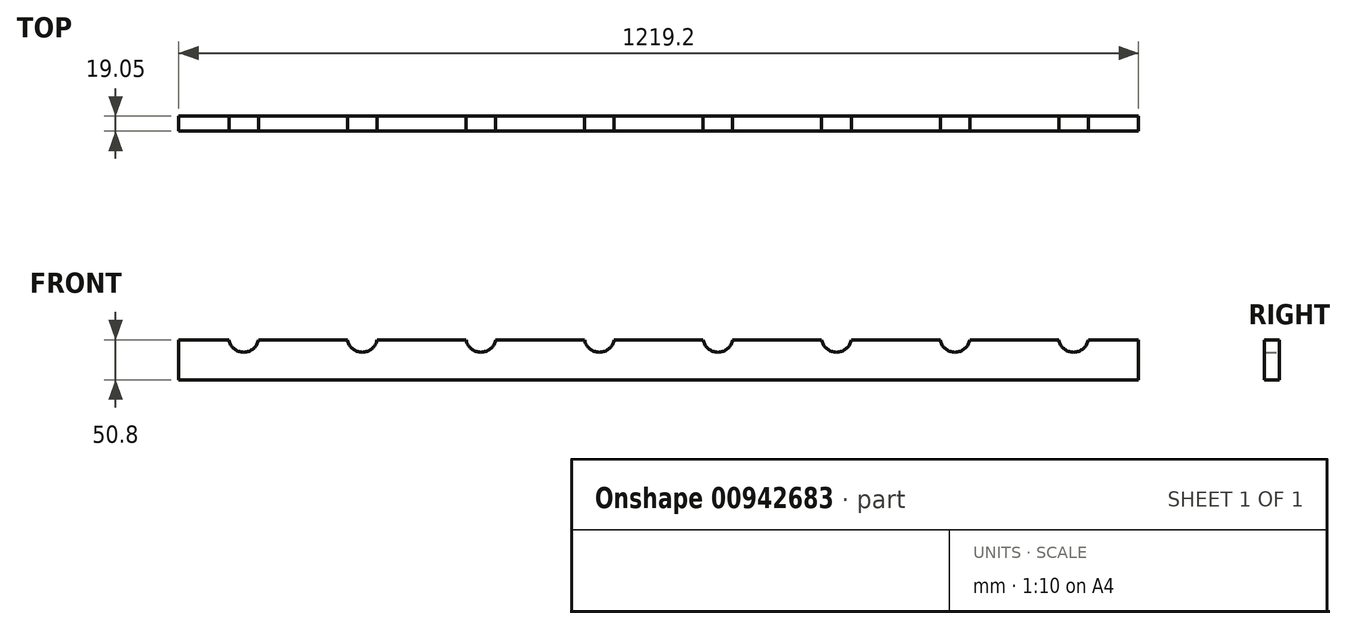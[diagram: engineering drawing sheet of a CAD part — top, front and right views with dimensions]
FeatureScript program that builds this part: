
annotation { "Feature Type Name" : "Feature", "Feature Type Description" : "" }
export const myFeature = defineFeature(function(context is Context, id is Id, definition is map)
    precondition{}
    {
        {
            var Q0;
            Q0=qCreatedBy(makeId("Front.planeOp"),FACE);
            var sketch = newSketch(context, id + "F0", { "sketchPlane" : qUnion([Q0])});
            skLineSegment(sketch, "E0.bottom", {"start": v(609.6, -25.4) * mm, "end": v(-609.6, -25.4) * mm});
            skLineSegment(sketch, "E0.top", {"start": v(609.6, 25.4) * mm, "end": v(545.83, 25.4) * mm});
            skLineSegment(sketch, "E0.left", {"start": v(609.6, -25.4) * mm, "end": v(609.6, 25.4) * mm});
            skLineSegment(sketch, "E0.right", {"start": v(-609.6, -25.4) * mm, "end": v(-609.6, 25.4) * mm});
            skPoint(sketch, "E0.middle", {"position": v(0, 0) * mm});
            skArc(sketch, "E1", {"start": v(-545.83, 25.4) * mm, "mid": v(-527.05, 9.53) * mm, "end": v(-508.27, 25.4) * mm});
            skArc(sketch, "E2.1.0.0", {"start": v(-395.25, 25.4) * mm, "mid": v(-376.46, 9.53) * mm, "end": v(-357.68, 25.4) * mm});
            skArc(sketch, "E2.2.0.0", {"start": v(-244.66, 25.4) * mm, "mid": v(-225.88, 9.53) * mm, "end": v(-207.1, 25.4) * mm});
            skArc(sketch, "E2.3.0.0", {"start": v(-94.08, 25.4) * mm, "mid": v(-75.3, 9.53) * mm, "end": v(-56.5, 25.4) * mm});
            skArc(sketch, "E2.4.0.0", {"start": v(56.5, 25.4) * mm, "mid": v(75.3, 9.53) * mm, "end": v(94.08, 25.4) * mm});
            skArc(sketch, "E2.5.0.0", {"start": v(207.1, 25.4) * mm, "mid": v(225.88, 9.53) * mm, "end": v(244.66, 25.4) * mm});
            skArc(sketch, "E2.6.0.0", {"start": v(357.68, 25.4) * mm, "mid": v(376.46, 9.53) * mm, "end": v(395.25, 25.4) * mm});
            skArc(sketch, "E2.7.0.0", {"start": v(508.27, 25.4) * mm, "mid": v(527.05, 9.52) * mm, "end": v(545.83, 25.4) * mm});
            skLineSegment(sketch, "E2.direction1", {"start": v(-527.05, 28.58) * mm, "end": v(-376.46, 28.58) * mm, "construction": true});
            skLineSegment(sketch, "E3.trimOffspring", {"start": v(508.27, 25.4) * mm, "end": v(395.25, 25.4) * mm});
            skLineSegment(sketch, "E4.trimOffspring", {"start": v(357.68, 25.4) * mm, "end": v(244.66, 25.4) * mm});
            skLineSegment(sketch, "E5.trimOffspring", {"start": v(207.1, 25.4) * mm, "end": v(94.08, 25.4) * mm});
            skLineSegment(sketch, "E6.trimOffspring", {"start": v(56.5, 25.4) * mm, "end": v(-56.5, 25.4) * mm});
            skLineSegment(sketch, "E7.trimOffspring", {"start": v(-94.08, 25.4) * mm, "end": v(-207.1, 25.4) * mm});
            skLineSegment(sketch, "E8.trimOffspring", {"start": v(-244.66, 25.4) * mm, "end": v(-357.68, 25.4) * mm});
            skLineSegment(sketch, "E9.trimOffspring", {"start": v(-395.25, 25.4) * mm, "end": v(-508.27, 25.4) * mm});
            skLineSegment(sketch, "E10.trimOffspring", {"start": v(-545.83, 25.4) * mm, "end": v(-609.6, 25.4) * mm});
            skSolve(sketch);
        }
        {
            var Q0;
            Q0=makeQuery(id+"F0.imprint","IMPRINT",FACE,{"disambiguationData":[TD([[makeQuery(id+"F0.imprint","IMPRINT",EDGE,{"derivedFrom":sQuery(id+"F0.wireOp",EDGE,"E0.bottom")}),-1.0]])]});
            extrude(context, id + "F1", {"entities" : qUnion([Q0]), "depth" : 19.05 * mm, "offsetDistance" : 25.4 * mm});
        }
    });
